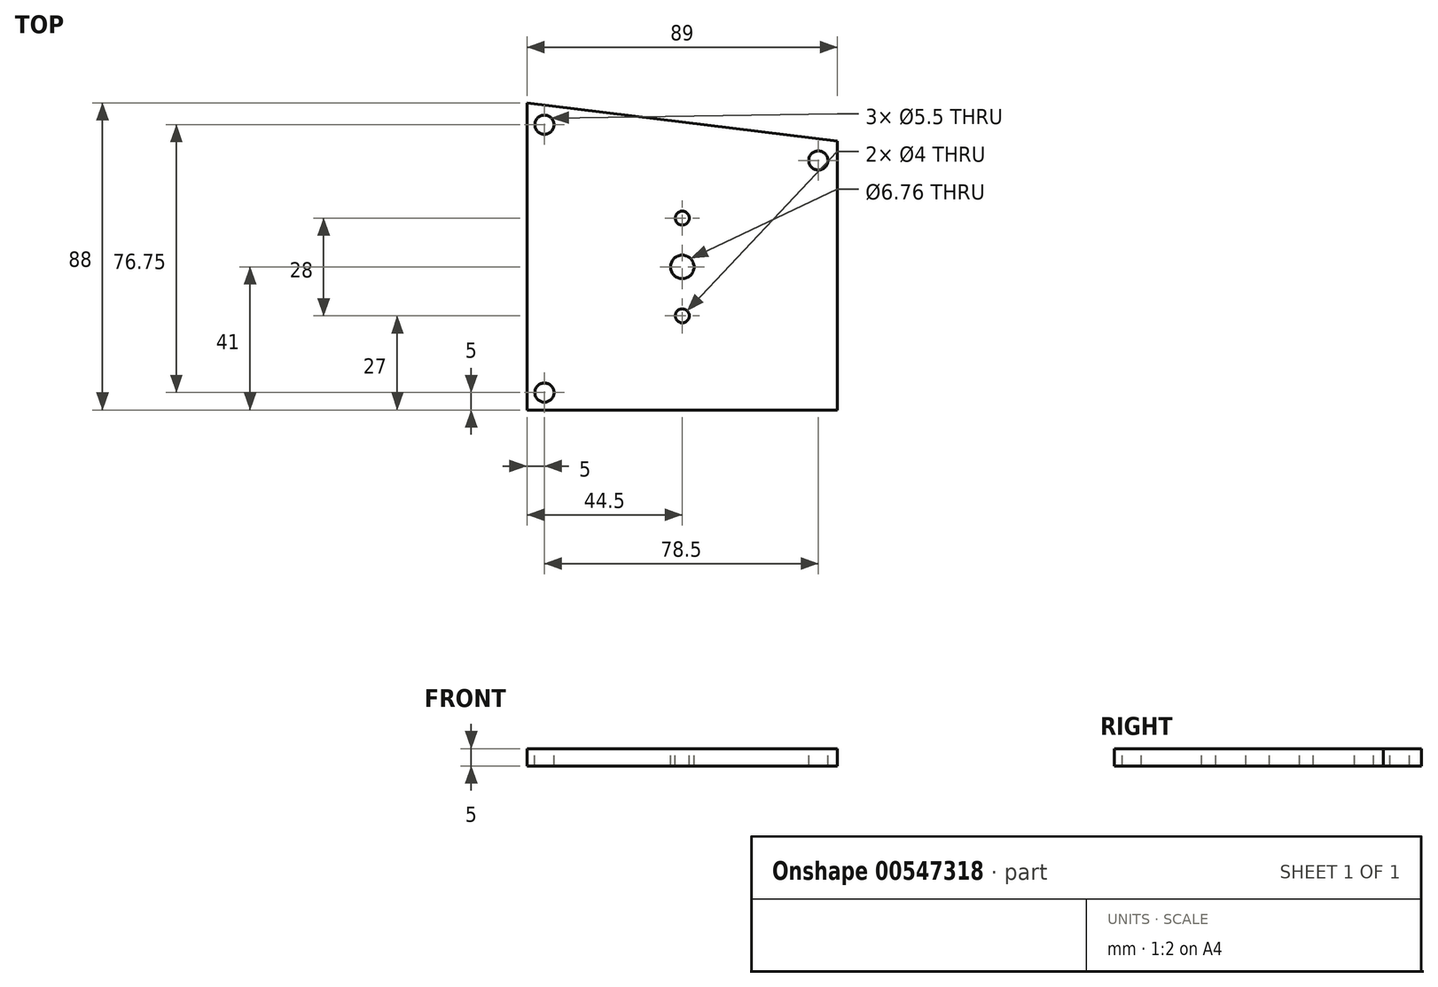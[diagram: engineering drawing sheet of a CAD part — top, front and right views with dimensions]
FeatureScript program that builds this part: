
annotation { "Feature Type Name" : "Feature", "Feature Type Description" : "" }
export const myFeature = defineFeature(function(context is Context, id is Id, definition is map)
    precondition{}
    {
        {
            var Q0;
            Q0=qCreatedBy(makeId("Top.planeOp"),FACE);
            var sketch = newSketch(context, id + "F0", { "sketchPlane" : qUnion([Q0])});
            skLineSegment(sketch, "E0", {"start": v(0, 0) * mm, "end": v(89, 0) * mm});
            skLineSegment(sketch, "E1", {"start": v(89, 0) * mm, "end": v(89, 77) * mm});
            skLineSegment(sketch, "E2", {"start": v(89, 77) * mm, "end": v(0, 88) * mm});
            skLineSegment(sketch, "E3", {"start": v(0, 88) * mm, "end": v(0, 0) * mm});
            skPoint(sketch, "E4", {"position": v(4, 4) * mm});
            skSolve(sketch);
        }
        {
            var Q0;
            Q0=makeQuery(id+"F0.imprint","IMPRINT",FACE,{"disambiguationData":[TD([[makeQuery(id+"F0.imprint","IMPRINT",EDGE,{"derivedFrom":sQuery(id+"F0.wireOp",EDGE,"E0")}),1.0]])]});
            extrude(context, id + "F1", {"entities" : qUnion([Q0]), "oppositeDirection" : true, "depth" : 5 * mm, "offsetDistance" : 25 * mm});
        }
        {
            var Q0;
            Q0=makeQuery(id+"F1.opExtrude","CAP_FACE",FACE,{"disambiguationData":[OSD([sQuery(id+"F0.wireOp",EDGE,"E0"),sQuery(id+"F0.wireOp",EDGE,"E1"),sQuery(id+"F0.wireOp",EDGE,"E2"),sQuery(id+"F0.wireOp",EDGE,"E3")])],"isStart":true});
            var sketch = newSketch(context, id + "F2", { "sketchPlane" : qUnion([Q0])});
            skPoint(sketch, "E5", {"position": v(5, 5) * mm});
            skPoint(sketch, "E6", {"position": v(5, 81.75) * mm});
            skPoint(sketch, "E7", {"position": v(83.5, 71.5) * mm});
            skSolve(sketch);
        }
        {
            var Q0;
            Q0=sQuery(id+"F2.wireOp",VERTEX,"E5");
            var Q1;
            Q1=sQuery(id+"F2.wireOp",VERTEX,"E6");
            var Q2;
            Q2=sQuery(id+"F2.wireOp",VERTEX,"E7");
            var Q3;
            Q3=makeQuery(id+"F1.opExtrude","SWEPT_BODY",BODY,{"disambiguationData":[OSD([sQuery(id+"F0.wireOp",EDGE,"E0"),sQuery(id+"F0.wireOp",EDGE,"E1"),sQuery(id+"F0.wireOp",EDGE,"E2"),sQuery(id+"F0.wireOp",EDGE,"E3")])]});
            hole(context, id + "F3", {"style" : HoleStyle.SIMPLE, "endStyle" : HoleEndStyle.THROUGH, "standardTappedOrClearance" : lookupTablePath({ "standard" : "ISO", "fit" : "Normal", "size" : "M5", "type" : "Clearance" }), "standardBlindInLast" : lookupTablePath({ "fit" : "Standard", "standard" : "ISO", "size" : "M5", "type" : "Clearance" }), "holeDiameter" : 5.5 * mm, "isTappedThrough" : true, "tappedDepth" : 12 * mm, "tapClearance" : 3, "locations" : qUnion([Q0, Q1, Q2]), "scope" : qUnion([Q3])});
        }
        {
            var Q0;
            Q0=makeQuery(id+"F1.opExtrude","CAP_FACE",FACE,{"disambiguationData":[OSD([sQuery(id+"F0.wireOp",EDGE,"E0"),sQuery(id+"F0.wireOp",EDGE,"E1"),sQuery(id+"F0.wireOp",EDGE,"E2"),sQuery(id+"F0.wireOp",EDGE,"E3")])],"isStart":true});
            var sketch = newSketch(context, id + "F4", { "sketchPlane" : qUnion([Q0])});
            skPoint(sketch, "E8", {"position": v(44.5, 41) * mm});
            skSolve(sketch);
        }
        {
            var Q0;
            Q0=sQuery(id+"F4.wireOp",VERTEX,"E8");
            var Q1;
            Q1=makeQuery(id+"F1.opExtrude","SWEPT_BODY",BODY,{"disambiguationData":[OSD([sQuery(id+"F0.wireOp",EDGE,"E0"),sQuery(id+"F0.wireOp",EDGE,"E1"),sQuery(id+"F0.wireOp",EDGE,"E2"),sQuery(id+"F0.wireOp",EDGE,"E3")])]});
            hole(context, id + "F5", {"style" : HoleStyle.SIMPLE, "endStyle" : HoleEndStyle.THROUGH, "standardTappedOrClearance" : lookupTablePath({ "standard" : "ANSI", "fit" : "Normal (ASME)", "size" : "1/4", "type" : "Clearance" }), "standardBlindInLast" : lookupTablePath({ "fit" : "Free", "standard" : "ANSI", "size" : "1/4", "type" : "Clearance" }), "holeDiameter" : 6.76 * mm, "isTappedThrough" : true, "tappedDepth" : 12 * mm, "tapClearance" : 3, "locations" : qUnion([Q0]), "scope" : qUnion([Q1])});
        }
        {
            var Q0;
            Q0=makeQuery(id+"F1.opExtrude","CAP_FACE",FACE,{"disambiguationData":[OSD([sQuery(id+"F0.wireOp",EDGE,"E0"),sQuery(id+"F0.wireOp",EDGE,"E1"),sQuery(id+"F0.wireOp",EDGE,"E2"),sQuery(id+"F0.wireOp",EDGE,"E3")])],"isStart":true});
            var sketch = newSketch(context, id + "F6", { "sketchPlane" : qUnion([Q0])});
            skPoint(sketch, "E9", {"position": v(44.5, 55) * mm});
            skPoint(sketch, "E10", {"position": v(44.5, 27) * mm});
            skSolve(sketch);
        }
        {
            var Q0;
            Q0=sQuery(id+"F6.wireOp",VERTEX,"E9");
            var Q1;
            Q1=sQuery(id+"F6.wireOp",VERTEX,"E10");
            var Q2;
            Q2=makeQuery(id+"F1.opExtrude","SWEPT_BODY",BODY,{"disambiguationData":[OSD([sQuery(id+"F0.wireOp",EDGE,"E0"),sQuery(id+"F0.wireOp",EDGE,"E1"),sQuery(id+"F0.wireOp",EDGE,"E2"),sQuery(id+"F0.wireOp",EDGE,"E3")])]});
            hole(context, id + "F7", {"style" : HoleStyle.SIMPLE, "endStyle" : HoleEndStyle.THROUGH, "holeDiameter" : 4 * mm, "isTappedThrough" : true, "tappedDepth" : 12 * mm, "tapClearance" : 3, "locations" : qUnion([Q0, Q1]), "scope" : qUnion([Q2])});
        }
    });
